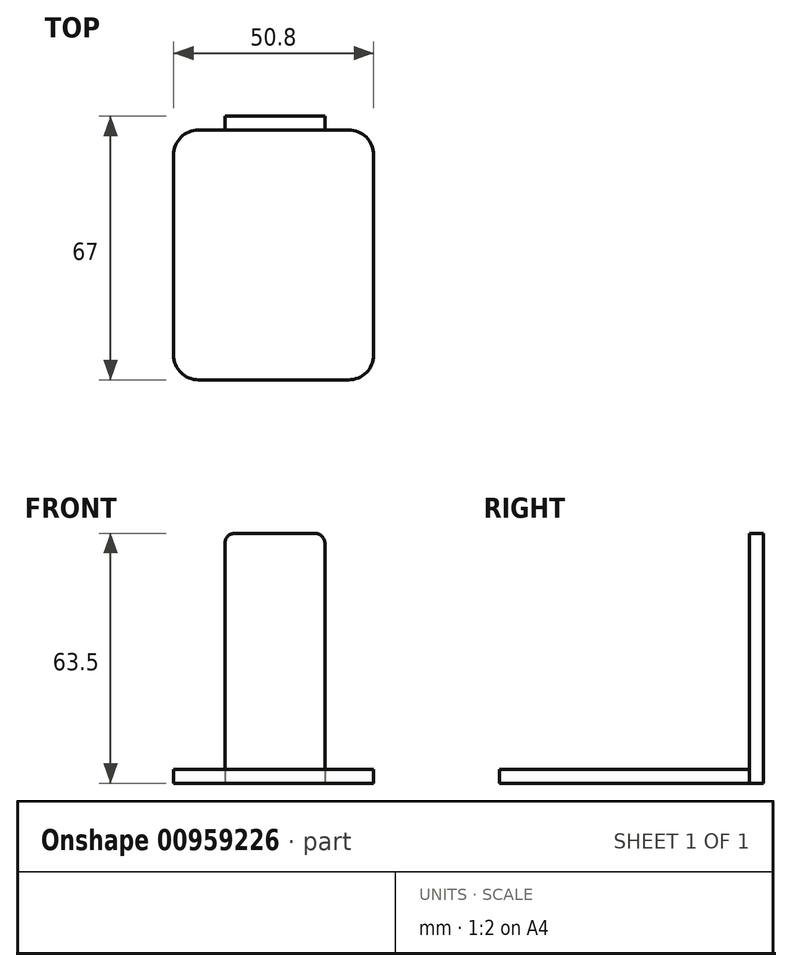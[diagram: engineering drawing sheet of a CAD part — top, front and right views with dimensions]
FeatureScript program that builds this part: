
annotation { "Feature Type Name" : "Feature", "Feature Type Description" : "" }
export const myFeature = defineFeature(function(context is Context, id is Id, definition is map)
    precondition{}
    {
        {
            var Q0;
            Q0=qCreatedBy(makeId("Top.planeOp"),FACE);
            var sketch = newSketch(context, id + "F0", { "sketchPlane" : qUnion([Q0])});
            skLineSegment(sketch, "E0.bottom", {"start": v(19.05, -63.5) * mm, "end": v(-19.05, -63.5) * mm});
            skLineSegment(sketch, "E0.top", {"start": v(19.05, 0) * mm, "end": v(-19.05, 0) * mm});
            skLineSegment(sketch, "E0.left", {"start": v(25.4, -57.15) * mm, "end": v(25.4, -6.35) * mm});
            skLineSegment(sketch, "E0.right", {"start": v(-25.4, -57.15) * mm, "end": v(-25.4, -6.35) * mm});
            skPoint(sketch, "E0.middle", {"position": v(0, 0) * mm});
            skPoint(sketch, "E1.visualSharp", {"position": v(25.4, -63.5) * mm});
            skArc(sketch, "E1.filletArc", {"start": v(19.05, -63.5) * mm, "mid": v(23.54, -61.64) * mm, "end": v(25.4, -57.15) * mm});
            skPoint(sketch, "E2.visualSharp", {"position": v(-25.4, -63.5) * mm});
            skArc(sketch, "E2.filletArc", {"start": v(-25.4, -57.15) * mm, "mid": v(-23.54, -61.64) * mm, "end": v(-19.05, -63.5) * mm});
            skPoint(sketch, "E3.visualSharp", {"position": v(-25.4, 0) * mm});
            skArc(sketch, "E3.filletArc", {"start": v(-19.05, 0) * mm, "mid": v(-23.54, -1.86) * mm, "end": v(-25.4, -6.35) * mm});
            skPoint(sketch, "E4.visualSharp", {"position": v(25.4, 0) * mm});
            skArc(sketch, "E4.filletArc", {"start": v(25.4, -6.35) * mm, "mid": v(23.54, -1.86) * mm, "end": v(19.05, 0) * mm});
            skSolve(sketch);
        }
        {
            var Q0;
            Q0=qCreatedBy(makeId("Front.planeOp"),FACE);
            var sketch = newSketch(context, id + "F1", { "sketchPlane" : qUnion([Q0])});
            skLineSegment(sketch, "E5.bottom", {"start": v(-9.86, 63.5) * mm, "end": v(10.46, 63.5) * mm});
            skLineSegment(sketch, "E5.top", {"start": v(-12.4, 0) * mm, "end": v(13, 0) * mm});
            skLineSegment(sketch, "E5.left", {"start": v(-12.4, 60.96) * mm, "end": v(-12.4, 0) * mm});
            skLineSegment(sketch, "E5.right", {"start": v(13, 60.96) * mm, "end": v(13, 0) * mm});
            skPoint(sketch, "E6.visualSharp", {"position": v(-12.4, 63.5) * mm});
            skArc(sketch, "E6.filletArc", {"start": v(-9.86, 63.5) * mm, "mid": v(-11.65, 62.76) * mm, "end": v(-12.4, 60.96) * mm});
            skPoint(sketch, "E7.visualSharp", {"position": v(13, 63.5) * mm});
            skArc(sketch, "E7.filletArc", {"start": v(13, 60.96) * mm, "mid": v(12.26, 62.76) * mm, "end": v(10.46, 63.5) * mm});
            skSolve(sketch);
        }
        {
            var Q0;
            Q0=makeQuery(id+"F0.imprint","IMPRINT",FACE,{"disambiguationData":[TD([[makeQuery(id+"F0.imprint","IMPRINT",EDGE,{"derivedFrom":sQuery(id+"F0.wireOp",EDGE,"E0.bottom")}),-1.0]])]});
            extrude(context, id + "F2", {"entities" : qUnion([Q0]), "depth" : 3.5 * mm, "offsetDistance" : 25.4 * mm});
        }
        {
            var Q0;
            Q0=makeQuery(id+"F1.imprint","IMPRINT",FACE,{"disambiguationData":[TD([[makeQuery(id+"F1.imprint","IMPRINT",EDGE,{"derivedFrom":sQuery(id+"F1.wireOp",EDGE,"E5.bottom")}),-1.0]])]});
            extrude(context, id + "F3", {"entities" : qUnion([Q0]), "operationType" : NewBodyOperationType.ADD, "oppositeDirection" : true, "depth" : 3.5 * mm, "offsetDistance" : 25.4 * mm});
        }
    });
